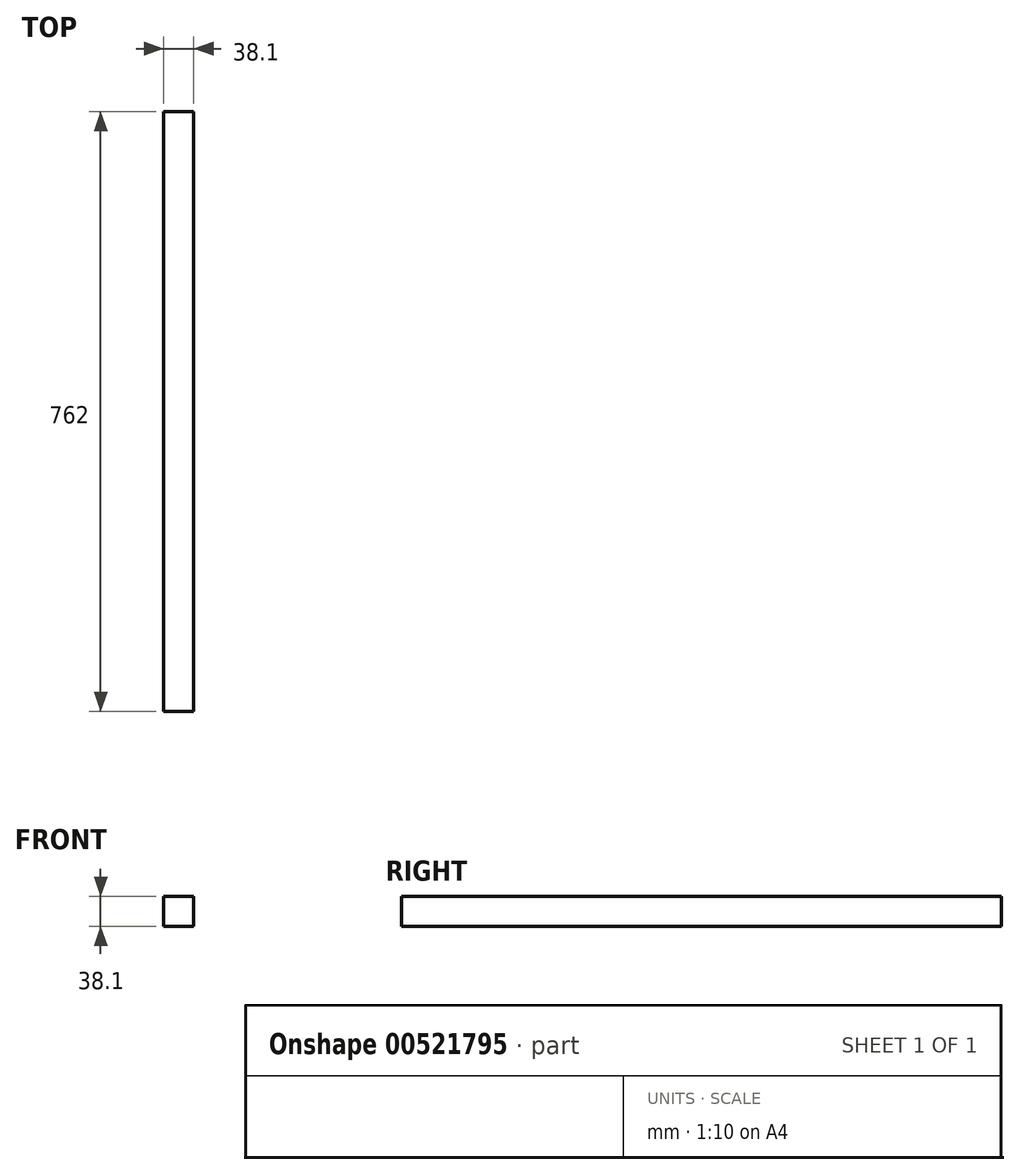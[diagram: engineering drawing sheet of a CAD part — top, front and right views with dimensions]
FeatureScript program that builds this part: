
annotation { "Feature Type Name" : "Feature", "Feature Type Description" : "" }
export const myFeature = defineFeature(function(context is Context, id is Id, definition is map)
    precondition{}
    {
        {
            var Q0;
            Q0=qCreatedBy(makeId("Front.planeOp"),FACE);
            var sketch = newSketch(context, id + "F0", { "sketchPlane" : qUnion([Q0])});
            skLineSegment(sketch, "E0.bottom", {"start": v(0, 0) * mm, "end": v(38.1, 0) * mm});
            skLineSegment(sketch, "E0.top", {"start": v(0, 38.1) * mm, "end": v(38.1, 38.1) * mm});
            skLineSegment(sketch, "E0.left", {"start": v(0, 0) * mm, "end": v(0, 38.1) * mm});
            skLineSegment(sketch, "E0.right", {"start": v(38.1, 0) * mm, "end": v(38.1, 38.1) * mm});
            skSolve(sketch);
        }
        {
            var Q0;
            Q0 = qSketchRegion(id + "F0", true);
            extrude(context, id + "F1", {"entities" : qUnion([Q0]), "oppositeDirection" : true, "depth" : 762 * mm, "offsetDistance" : 25.4 * mm});
        }
    });
